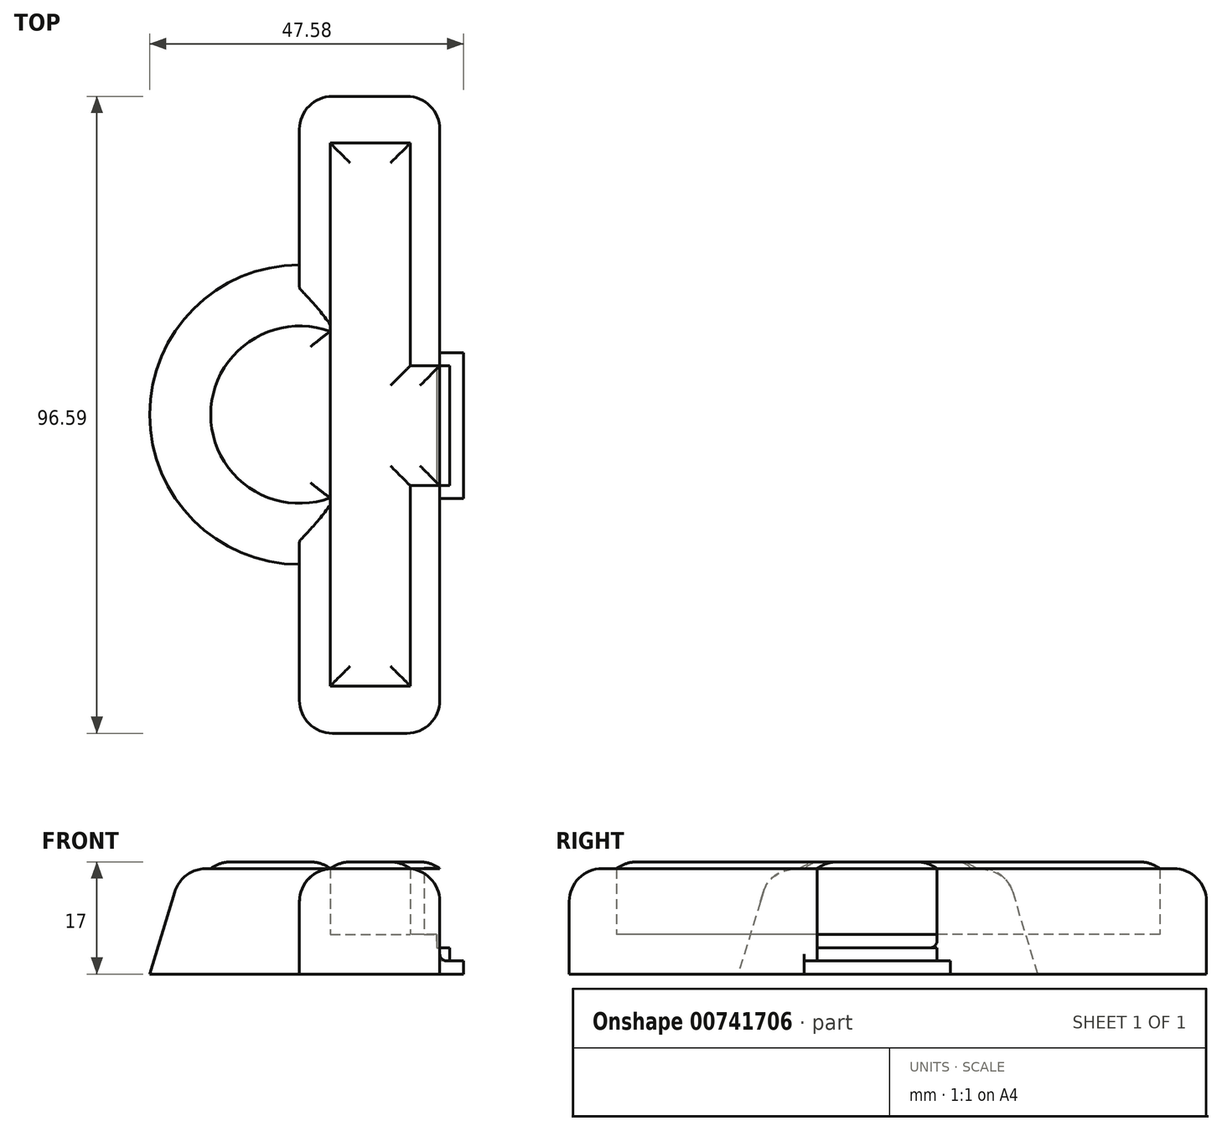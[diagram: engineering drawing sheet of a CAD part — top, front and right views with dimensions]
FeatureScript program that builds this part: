
annotation { "Feature Type Name" : "Feature", "Feature Type Description" : "" }
export const myFeature = defineFeature(function(context is Context, id is Id, definition is map)
    precondition{}
    {
        {
            var Q0;
            Q0=qCreatedBy(makeId("Top.planeOp"),FACE);
            var sketch = newSketch(context, id + "F0", { "sketchPlane" : qUnion([Q0])});
            skLineSegment(sketch, "E0.bottom", {"start": v(0, 48.27) * mm, "end": v(21.27, 48.27) * mm});
            skLineSegment(sketch, "E0.top", {"start": v(0, -48.32) * mm, "end": v(21.27, -48.32) * mm});
            skLineSegment(sketch, "E0.left", {"start": v(0, 48.27) * mm, "end": v(0, -48.32) * mm});
            skLineSegment(sketch, "E0.right", {"start": v(21.27, 48.27) * mm, "end": v(21.27, -48.32) * mm});
            skSolve(sketch);
        }
        {
            var Q0;
            Q0=makeQuery(id+"F0.imprint","IMPRINT",FACE,{"disambiguationData":[TD([[makeQuery(id+"F0.imprint","IMPRINT",EDGE,{"derivedFrom":sQuery(id+"F0.wireOp",EDGE,"E0.bottom")}),-1.0]])]});
            extrude(context, id + "F1", {"entities" : qUnion([Q0]), "depth" : 3 * mm, "offsetDistance" : 25 * mm});
        }
        {
            var Q0;
            Q0=makeQuery(id+"F1.opExtrude","CAP_FACE",FACE,{"disambiguationData":[OSD([sQuery(id+"F0.wireOp",EDGE,"E0.bottom"),sQuery(id+"F0.wireOp",EDGE,"E0.top"),sQuery(id+"F0.wireOp",EDGE,"E0.left"),sQuery(id+"F0.wireOp",EDGE,"E0.right")])],"isStart":false});
            var sketch = newSketch(context, id + "F2", { "sketchPlane" : qUnion([Q0])});
            skLineSegment(sketch, "E1.bottom", {"start": v(4.68, 41.18) * mm, "end": v(16.78, 41.18) * mm});
            skLineSegment(sketch, "E1.top", {"start": v(4.68, -41.14) * mm, "end": v(16.78, -41.14) * mm});
            skLineSegment(sketch, "E1.left", {"start": v(4.68, 41.18) * mm, "end": v(4.68, -41.14) * mm});
            skLineSegment(sketch, "E1.right", {"start": v(16.78, 41.18) * mm, "end": v(16.78, -41.14) * mm});
            skSolve(sketch);
        }
        {
            var Q0;
            Q0=makeQuery(id+"F2.imprint","IMPRINT",FACE,{"disambiguationData":[TD([[makeQuery(id+"F2.imprint","IMPRINT",EDGE,{"derivedFrom":sQuery(id+"F2.wireOp",EDGE,"E1.bottom")}),-1.0]])]});
            extrude(context, id + "F3", {"entities" : qUnion([Q0]), "operationType" : NewBodyOperationType.ADD, "depth" : 3 * mm, "offsetDistance" : 25 * mm});
        }
        {
            var Q0;
            Q0=makeQuery(id+"F2.imprint","IMPRINT",FACE,{"disambiguationData":[TD([[makeQuery(id+"F2.imprint","IMPRINT",EDGE,{"derivedFrom":sQuery(id+"F2.wireOp",EDGE,"E1.bottom")}),1.0]])]});
            var sketch = newSketch(context, id + "F4", { "sketchPlane" : qUnion([Q0])});
            skLineSegment(sketch, "E2.bottom", {"start": v(16.62, 7.41) * mm, "end": v(18.88, 7.41) * mm});
            skLineSegment(sketch, "E2.top", {"start": v(16.62, -10.75) * mm, "end": v(18.88, -10.75) * mm});
            skLineSegment(sketch, "E2.left", {"start": v(16.62, 7.41) * mm, "end": v(16.62, -10.75) * mm});
            skLineSegment(sketch, "E2.right", {"start": v(18.88, 7.41) * mm, "end": v(18.88, -10.75) * mm});
            skSolve(sketch);
        }
        {
            var Q0;
            {var subQ1=sQuery(id+"F4.wireOp",EDGE,"E2.right");Q0=makeQuery(id+"F4.imprint","IMPRINT",FACE,{"disambiguationData":[TD([[makeQuery(id+"F4.imprint","IMPRINT",EDGE,{"derivedFrom":subQ1}),1.0]])]});}
            extrude(context, id + "F5", {"entities" : qUnion([Q0]), "operationType" : NewBodyOperationType.ADD, "depth" : 13 * mm, "offsetDistance" : 25 * mm});
        }
        {
            var Q0;
            Q0=makeQuery(id+"F5.opExtrude","CAP_FACE",FACE,{"disambiguationData":[OSD([sQuery(id+"F0.wireOp",EDGE,"E0.bottom"),sQuery(id+"F0.wireOp",EDGE,"E0.top"),sQuery(id+"F0.wireOp",EDGE,"E0.left"),sQuery(id+"F0.wireOp",EDGE,"E0.right"),sQuery(id+"F2.wireOp",EDGE,"E1.bottom"),sQuery(id+"F2.wireOp",EDGE,"E1.top"),sQuery(id+"F2.wireOp",EDGE,"E1.left"),sQuery(id+"F2.wireOp",EDGE,"E1.right"),sQuery(id+"F4.wireOp",EDGE,"E2.bottom"),sQuery(id+"F4.wireOp",EDGE,"E2.top"),sQuery(id+"F4.wireOp",EDGE,"E2.right")])],"isStart":false});
            var sketch = newSketch(context, id + "F6", { "sketchPlane" : qUnion([Q0])});
            skArc(sketch, "E3", {"start": v(0, 17.81) * mm, "mid": v(-17.81, 0) * mm, "end": v(0, -17.81) * mm});
            skSolve(sketch);
        }
        {
            var Q0;
            {var subQ0=sQuery(id+"F6.wireOp",EDGE,"E3");Q0=makeQuery(id+"F6.imprint","IMPRINT",FACE,{"disambiguationData":[TD([[makeQuery(id+"F6.imprint","IMPRINT",EDGE,{"derivedFrom":subQ0}),1.0]])]});}
            extrude(context, id + "F7", {"entities" : qUnion([Q0]), "operationType" : NewBodyOperationType.ADD, "depth" : -16 * mm, "offsetDistance" : 25 * mm, "hasDraft" : true, "draftAngle" : 17 * degree});
        }
        {
            var Q0;
            {var subQ0=sQuery(id+"F0.wireOp",EDGE,"E0.left");Q0=makeQuery(id+"F7.boolean.opBoolean","MERGE",FACE,{"derivedFrom":[makeQuery(id+"F5.opExtrude","CAP_FACE",FACE,{"disambiguationData":[OSD([sQuery(id+"F0.wireOp",EDGE,"E0.bottom"),sQuery(id+"F0.wireOp",EDGE,"E0.top"),subQ0,sQuery(id+"F0.wireOp",EDGE,"E0.right"),sQuery(id+"F2.wireOp",EDGE,"E1.bottom"),sQuery(id+"F2.wireOp",EDGE,"E1.top"),sQuery(id+"F2.wireOp",EDGE,"E1.left"),sQuery(id+"F2.wireOp",EDGE,"E1.right"),sQuery(id+"F4.wireOp",EDGE,"E2.bottom"),sQuery(id+"F4.wireOp",EDGE,"E2.top"),sQuery(id+"F4.wireOp",EDGE,"E2.right")])],"isStart":false}),makeQuery(id+"F7.opExtrude","CAP_FACE",FACE,{"disambiguationData":[OSD([subQ0,sQuery(id+"F6.wireOp",EDGE,"E3")])],"isStart":true})]});}
            var sketch = newSketch(context, id + "F8", { "sketchPlane" : qUnion([Q0])});
            skLineSegment(sketch, "E4.bottom", {"start": v(18.88, 7.41) * mm, "end": v(21.27, 7.41) * mm});
            skLineSegment(sketch, "E4.top", {"start": v(18.88, -10.74) * mm, "end": v(21.27, -10.74) * mm});
            skLineSegment(sketch, "E4.left", {"start": v(18.88, 7.41) * mm, "end": v(18.88, -10.74) * mm});
            skLineSegment(sketch, "E4.right", {"start": v(21.27, 7.41) * mm, "end": v(21.27, -10.74) * mm});
            skSolve(sketch);
        }
        {
            var Q0;
            Q0=makeQuery(id+"F8.imprint","IMPRINT",FACE,{"disambiguationData":[TD([[makeQuery(id+"F8.imprint","IMPRINT",EDGE,{"derivedFrom":sQuery(id+"F8.wireOp",EDGE,"E4.bottom")}),-1.0]])]});
            extrude(context, id + "F9", {"entities" : qUnion([Q0]), "operationType" : NewBodyOperationType.REMOVE, "oppositeDirection" : true, "depth" : 25 * mm, "offsetDistance" : 25 * mm});
        }
        {
            var Q0;
            Q0=makeQuery(id+"F3.opExtrude","SWEPT_FACE",FACE,{"disambiguationData":[OSD([sQuery(id+"F2.wireOp",EDGE,"E1.right")])]});
            var Q1;
            Q1=makeQuery(id+"F9.boolean.opBoolean","COPY",FACE,{"derivedFrom":makeQuery(id+"F9.opExtrude","SWEPT_FACE",FACE,{"disambiguationData":[OSD([sQuery(id+"F8.wireOp",EDGE,"E4.left")])]})});
            extrude(context, id + "F10", {"entities" : qUnion([Q0, Q1]), "operationType" : NewBodyOperationType.ADD, "depth" : 6 * mm, "offsetDistance" : 25 * mm});
        }
        {
            var Q0;
            Q0=makeQuery(id+"F10.opExtrude","SWEPT_FACE",FACE,{"disambiguationData":[OSD([sQuery(id+"F4.wireOp",EDGE,"E2.right"),sQuery(id+"F8.wireOp",EDGE,"E4.top"),sQuery(id+"F8.wireOp",EDGE,"E4.left")])]});
            extrude(context, id + "F11", {"entities" : qUnion([Q0]), "operationType" : NewBodyOperationType.ADD, "depth" : 2 * mm, "offsetDistance" : 25 * mm});
        }
        {
            var Q0;
            {var subQ0=sQuery(id+"F4.wireOp",EDGE,"E2.bottom");Q0=makeQuery(id+"F10.boolean.opBoolean","MERGE",FACE,{"derivedFrom":[makeQuery(id+"F10.opExtrude","SWEPT_FACE",FACE,{"disambiguationData":[OSD([sQuery(id+"F2.wireOp",EDGE,"E1.right"),subQ0])]}),makeQuery(id+"F10.opExtrude","SWEPT_FACE",FACE,{"disambiguationData":[OSD([subQ0,sQuery(id+"F8.wireOp",EDGE,"E4.bottom"),sQuery(id+"F8.wireOp",EDGE,"E4.left")])]})]});}
            var sketch = newSketch(context, id + "F12", { "sketchPlane" : qUnion([Q0])});
            skLineSegment(sketch, "E5.bottom", {"start": v(-24.88, 3) * mm, "end": v(-21.27, 3) * mm});
            skLineSegment(sketch, "E5.top", {"start": v(-24.88, 0) * mm, "end": v(-21.27, 0) * mm});
            skLineSegment(sketch, "E5.left", {"start": v(-24.88, 3) * mm, "end": v(-24.88, 0) * mm});
            skLineSegment(sketch, "E5.right", {"start": v(-21.27, 3) * mm, "end": v(-21.27, 0) * mm});
            skSolve(sketch);
        }
        {
            var Q0;
            Q0=makeQuery(id+"F12.imprint","IMPRINT",FACE,{"disambiguationData":[TD([[makeQuery(id+"F12.imprint","IMPRINT",EDGE,{"derivedFrom":sQuery(id+"F12.wireOp",EDGE,"E5.top")}),1.0]])]});
            extrude(context, id + "F13", {"entities" : qUnion([Q0]), "operationType" : NewBodyOperationType.ADD, "depth" : 2 * mm, "offsetDistance" : 25 * mm});
        }
        {
            var Q0;
            {var subQ0=sQuery(id+"F2.wireOp",EDGE,"E1.right");var subQ1=makeQuery(id+"F3.opExtrude","CAP_FACE",FACE,{"disambiguationData":[OSD([sQuery(id+"F2.wireOp",EDGE,"E1.bottom"),sQuery(id+"F2.wireOp",EDGE,"E1.top"),sQuery(id+"F2.wireOp",EDGE,"E1.left"),subQ0])],"isStart":false});Q0=makeQuery(id+"F10.boolean.opBoolean","MERGE",FACE,{"derivedFrom":[subQ1,makeQuery(id+"F10.opExtrude","SWEPT_FACE",FACE,{"disambiguationData":[OSD([subQ0]),TDD([makeQuery(id+"F5.boolean.opBoolean","SPLIT",EDGE,{"disambiguationData":[topologyDisambiguationEdgeConnected([makeQuery(id+"F3.opExtrude","SWEPT_FACE",FACE,{"disambiguationData":[OSD([subQ0])]})])],"derivedFrom":makeQuery(id+"F3.opExtrude","CAP_EDGE",EDGE,{"disambiguationData":[OSD([subQ0])],"isStart":false})})])]})]});}
            var sketch = newSketch(context, id + "F14", { "sketchPlane" : qUnion([Q0])});
            skLineSegment(sketch, "E6.bottom", {"start": v(16.78, 7.41) * mm, "end": v(22.78, 7.41) * mm});
            skLineSegment(sketch, "E6.top", {"start": v(16.78, -10.75) * mm, "end": v(22.78, -10.75) * mm});
            skLineSegment(sketch, "E6.left", {"start": v(16.78, 7.41) * mm, "end": v(16.78, -10.75) * mm});
            skLineSegment(sketch, "E6.right", {"start": v(22.78, 7.41) * mm, "end": v(22.78, -10.75) * mm});
            skSolve(sketch);
        }
        {
            var Q0;
            {var subQ0=sQuery(id+"F14.wireOp",EDGE,"E6.left");Q0=makeQuery(id+"F14.imprint","IMPRINT",FACE,{"disambiguationData":[TD([[makeQuery(id+"F14.imprint","IMPRINT",EDGE,{"derivedFrom":subQ0}),1.0]])]});}
            extrude(context, id + "F15", {"entities" : qUnion([Q0]), "operationType" : NewBodyOperationType.REMOVE, "depth" : -2 * mm, "offsetDistance" : 25 * mm});
        }
        {
            var Q0;
            {var subQ0=sQuery(id+"F4.wireOp",EDGE,"E2.right");Q0=makeQuery(id+"F13.boolean.opBoolean","MERGE",FACE,{"derivedFrom":[makeQuery(id+"F11.boolean.opBoolean","MERGE",FACE,{"derivedFrom":[makeQuery(id+"F10.opExtrude","SWEPT_FACE",FACE,{"disambiguationData":[OSD([subQ0])]}),makeQuery(id+"F11.opExtrude","SWEPT_FACE",FACE,{"disambiguationData":[OSD([sQuery(id+"F0.wireOp",EDGE,"E0.bottom"),sQuery(id+"F0.wireOp",EDGE,"E0.top"),sQuery(id+"F0.wireOp",EDGE,"E0.left"),sQuery(id+"F0.wireOp",EDGE,"E0.right"),subQ0,sQuery(id+"F8.wireOp",EDGE,"E4.top"),sQuery(id+"F8.wireOp",EDGE,"E4.left")])]})]}),makeQuery(id+"F13.opExtrude","SWEPT_FACE",FACE,{"disambiguationData":[OSD([sQuery(id+"F12.wireOp",EDGE,"E5.bottom")])]})]});}
            extrude(context, id + "F16", {"entities" : qUnion([Q0]), "operationType" : NewBodyOperationType.REMOVE, "oppositeDirection" : true, "depth" : 1 * mm, "offsetDistance" : 25 * mm});
        }
        {
            var Q0;
            {var subQ0=sQuery(id+"F0.wireOp",EDGE,"E0.left");Q0=makeQuery(id+"F7.boolean.opBoolean","MERGE",FACE,{"derivedFrom":[makeQuery(id+"F5.opExtrude","CAP_FACE",FACE,{"disambiguationData":[OSD([sQuery(id+"F0.wireOp",EDGE,"E0.bottom"),sQuery(id+"F0.wireOp",EDGE,"E0.top"),subQ0,sQuery(id+"F0.wireOp",EDGE,"E0.right"),sQuery(id+"F2.wireOp",EDGE,"E1.bottom"),sQuery(id+"F2.wireOp",EDGE,"E1.top"),sQuery(id+"F2.wireOp",EDGE,"E1.left"),sQuery(id+"F2.wireOp",EDGE,"E1.right"),sQuery(id+"F4.wireOp",EDGE,"E2.bottom"),sQuery(id+"F4.wireOp",EDGE,"E2.top"),sQuery(id+"F4.wireOp",EDGE,"E2.right")])],"isStart":false}),makeQuery(id+"F7.opExtrude","CAP_FACE",FACE,{"disambiguationData":[OSD([subQ0,sQuery(id+"F6.wireOp",EDGE,"E3")])],"isStart":true})]});}
            var sketch = newSketch(context, id + "F17", { "sketchPlane" : qUnion([Q0])});
            skLineSegment(sketch, "E7.bottom", {"start": v(0, -48.32) * mm, "end": v(21.27, -48.32) * mm});
            skLineSegment(sketch, "E7.top", {"start": v(0, 48.27) * mm, "end": v(21.27, 48.27) * mm});
            skLineSegment(sketch, "E7.left", {"start": v(0, -48.32) * mm, "end": v(0, 48.27) * mm});
            skLineSegment(sketch, "E7.right", {"start": v(21.27, -48.32) * mm, "end": v(21.27, 48.27) * mm});
            skSolve(sketch);
        }
        {
            var Q0;
            Q0=makeQuery(id+"F15.boolean.opBoolean","COPY",FACE,{"derivedFrom":makeQuery(id+"F15.opExtrude","SWEPT_FACE",FACE,{"disambiguationData":[OSD([sQuery(id+"F14.wireOp",EDGE,"E6.left")])]})});
            extrude(context, id + "F18", {"entities" : qUnion([Q0]), "operationType" : NewBodyOperationType.ADD, "depth" : 4 * mm, "offsetDistance" : 25 * mm});
        }
        {
            var Q0;
            {var subQ2=sQuery(id+"F4.wireOp",EDGE,"E2.top");Q0=makeQuery(id+"F17.imprint","IMPRINT",FACE,{"disambiguationData":[TD([[makeQuery(id+"F17.imprint","IMPRINT",EDGE,{"derivedFrom":makeQuery(id+"F5.opExtrude","CAP_EDGE",EDGE,{"disambiguationData":[OSD([subQ2])],"isStart":false})}),1.0]])]});}
            extrude(context, id + "F19", {"entities" : qUnion([Q0]), "depth" : 1 * mm, "offsetDistance" : 25 * mm});
        }
        {
            var Q0;
            {var subQ0=sQuery(id+"F0.wireOp",EDGE,"E0.left");Q0=makeQuery(id+"F7.boolean.opBoolean","MERGE",FACE,{"derivedFrom":[makeQuery(id+"F5.opExtrude","CAP_FACE",FACE,{"disambiguationData":[OSD([sQuery(id+"F0.wireOp",EDGE,"E0.bottom"),sQuery(id+"F0.wireOp",EDGE,"E0.top"),subQ0,sQuery(id+"F0.wireOp",EDGE,"E0.right"),sQuery(id+"F2.wireOp",EDGE,"E1.bottom"),sQuery(id+"F2.wireOp",EDGE,"E1.top"),sQuery(id+"F2.wireOp",EDGE,"E1.left"),sQuery(id+"F2.wireOp",EDGE,"E1.right"),sQuery(id+"F4.wireOp",EDGE,"E2.bottom"),sQuery(id+"F4.wireOp",EDGE,"E2.top"),sQuery(id+"F4.wireOp",EDGE,"E2.right")])],"isStart":false}),makeQuery(id+"F7.opExtrude","CAP_FACE",FACE,{"disambiguationData":[OSD([subQ0,sQuery(id+"F6.wireOp",EDGE,"E3")])],"isStart":true})]});}
            var sketch = newSketch(context, id + "F20", { "sketchPlane" : qUnion([Q0])});
            skArc(sketch, "E8", {"start": v(4.68, 12.6) * mm, "mid": v(-13.44, 0) * mm, "end": v(4.68, -12.6) * mm});
            skSolve(sketch);
        }
        {
            var Q0;
            {var subQ0=sQuery(id+"F20.wireOp",EDGE,"E8");Q0=makeQuery(id+"F20.imprint","IMPRINT",FACE,{"disambiguationData":[TD([[makeQuery(id+"F20.imprint","IMPRINT",EDGE,{"derivedFrom":subQ0}),1.0]])]});}
            extrude(context, id + "F21", {"entities" : qUnion([Q0]), "depth" : 1 * mm, "offsetDistance" : 25 * mm});
        }
        {
            var Q0;
            {var subQ0=sQuery(id+"F0.wireOp",EDGE,"E0.right");var subQ1=sQuery(id+"F0.wireOp",EDGE,"E0.bottom");Q0=makeQuery(id+"F5.boolean.opBoolean","MERGE",EDGE,{"derivedFrom":[makeQuery(id+"F1.opExtrude","SWEPT_EDGE",EDGE,{"disambiguationData":[OSD([subQ1,subQ0])]}),makeQuery(id+"F5.opExtrude","SWEPT_EDGE",EDGE,{"disambiguationData":[OSD([subQ1,subQ0])]})]});}
            var Q1;
            Q1=makeQuery(id+"F5.opExtrude","CAP_EDGE",EDGE,{"disambiguationData":[OSD([sQuery(id+"F0.wireOp",EDGE,"E0.bottom")])],"isStart":false});
            var Q2;
            {var subQ1=sQuery(id+"F0.wireOp",EDGE,"E0.right");var subQ3=sQuery(id+"F0.wireOp",EDGE,"E0.bottom");Q2=makeQuery(id+"F9.boolean.opBoolean","SPLIT",EDGE,{"disambiguationData":[TD([makeQuery(id+"F1.opExtrude","SWEPT_FACE",FACE,{"disambiguationData":[OSD([subQ3])]})])],"derivedFrom":makeQuery(id+"F5.opExtrude","CAP_EDGE",EDGE,{"disambiguationData":[OSD([subQ1])],"isStart":false})});}
            var Q3;
            {var subQ0=sQuery(id+"F0.wireOp",EDGE,"E0.right");var subQ1=sQuery(id+"F0.wireOp",EDGE,"E0.top");Q3=makeQuery(id+"F5.boolean.opBoolean","MERGE",EDGE,{"derivedFrom":[makeQuery(id+"F1.opExtrude","SWEPT_EDGE",EDGE,{"disambiguationData":[OSD([subQ1,subQ0])]}),makeQuery(id+"F5.opExtrude","SWEPT_EDGE",EDGE,{"disambiguationData":[OSD([subQ1,subQ0])]})]});}
            var Q4;
            {var subQ0=sQuery(id+"F0.wireOp",EDGE,"E0.top");var subQ1=sQuery(id+"F0.wireOp",EDGE,"E0.right");Q4=makeQuery(id+"F9.boolean.opBoolean","SPLIT",EDGE,{"disambiguationData":[TD([makeQuery(id+"F1.opExtrude","SWEPT_FACE",FACE,{"disambiguationData":[OSD([subQ0])]})])],"derivedFrom":makeQuery(id+"F5.opExtrude","CAP_EDGE",EDGE,{"disambiguationData":[OSD([subQ1])],"isStart":false})});}
            var Q5;
            Q5=makeQuery(id+"F5.opExtrude","CAP_EDGE",EDGE,{"disambiguationData":[OSD([sQuery(id+"F0.wireOp",EDGE,"E0.top")])],"isStart":false});
            var Q6;
            {var subQ0=sQuery(id+"F0.wireOp",EDGE,"E0.left");var subQ1=sQuery(id+"F0.wireOp",EDGE,"E0.bottom");Q6=makeQuery(id+"F7.boolean.opBoolean","SPLIT",EDGE,{"disambiguationData":[TD([makeQuery(id+"F1.opExtrude","SWEPT_FACE",FACE,{"disambiguationData":[OSD([subQ1])]})])],"derivedFrom":makeQuery(id+"F5.opExtrude","CAP_EDGE",EDGE,{"disambiguationData":[OSD([subQ0])],"isStart":false})});}
            var Q7;
            {var subQ0=sQuery(id+"F0.wireOp",EDGE,"E0.left");var subQ1=sQuery(id+"F0.wireOp",EDGE,"E0.bottom");Q7=makeQuery(id+"F5.boolean.opBoolean","MERGE",EDGE,{"derivedFrom":[makeQuery(id+"F1.opExtrude","SWEPT_EDGE",EDGE,{"disambiguationData":[OSD([subQ1,subQ0])]}),makeQuery(id+"F5.opExtrude","SWEPT_EDGE",EDGE,{"disambiguationData":[OSD([subQ1,subQ0])]})]});}
            var Q8;
            {var subQ0=sQuery(id+"F0.wireOp",EDGE,"E0.top");var subQ1=sQuery(id+"F0.wireOp",EDGE,"E0.left");Q8=makeQuery(id+"F7.boolean.opBoolean","SPLIT",EDGE,{"disambiguationData":[TD([makeQuery(id+"F1.opExtrude","SWEPT_FACE",FACE,{"disambiguationData":[OSD([subQ0])]})])],"derivedFrom":makeQuery(id+"F5.opExtrude","CAP_EDGE",EDGE,{"disambiguationData":[OSD([subQ1])],"isStart":false})});}
            var Q9;
            {var subQ0=sQuery(id+"F0.wireOp",EDGE,"E0.left");var subQ1=sQuery(id+"F0.wireOp",EDGE,"E0.top");Q9=makeQuery(id+"F5.boolean.opBoolean","MERGE",EDGE,{"derivedFrom":[makeQuery(id+"F1.opExtrude","SWEPT_EDGE",EDGE,{"disambiguationData":[OSD([subQ1,subQ0])]}),makeQuery(id+"F5.opExtrude","SWEPT_EDGE",EDGE,{"disambiguationData":[OSD([subQ1,subQ0])]})]});}
            var Q10;
            Q10=makeQuery(id+"F7.opExtrude","CAP_EDGE",EDGE,{"disambiguationData":[OSD([sQuery(id+"F6.wireOp",EDGE,"E3")])],"isStart":true});
            var Q11;
            Q11=makeQuery(id+"F19.opExtrude","CAP_EDGE",EDGE,{"disambiguationData":[OSD([sQuery(id+"F17.wireOp",EDGE,"E7.right")])],"isStart":false});
            var Q12;
            {var subQ0=sQuery(id+"F2.wireOp",EDGE,"E1.right");var subQ1=makeQuery(id+"F2.imprint","IMPRINT",EDGE,{"derivedFrom":subQ0});Q12=makeQuery(id+"F19.opExtrude","CAP_EDGE",EDGE,{"disambiguationData":[OSD([subQ0]),TDD([makeQuery(id+"F17.imprint","IMPRINT",EDGE,{"derivedFrom":makeQuery(id+"F5.opExtrude","CAP_EDGE",EDGE,{"disambiguationData":[OSD([subQ0]),TDD([makeQuery(id+"F4.imprint","IMPRINT",EDGE,{"disambiguationData":[TD([[makeQuery(id+"F4.imprint","INTERSECT",VERTEX,{"derivedFrom":[makeQuery(id+"F2.imprint","IMPRINT",EDGE,{"derivedFrom":sQuery(id+"F2.wireOp",EDGE,"E1.bottom")}),subQ1]}),-1.0]])],"derivedFrom":subQ1})])],"isStart":false})})])],"isStart":false});}
            var Q13;
            Q13=makeQuery(id+"F19.opExtrude","CAP_EDGE",EDGE,{"disambiguationData":[OSD([sQuery(id+"F4.wireOp",EDGE,"E2.bottom"),sQuery(id+"F8.wireOp",EDGE,"E4.bottom")])],"isStart":false});
            var Q14;
            Q14=makeQuery(id+"F19.opExtrude","CAP_EDGE",EDGE,{"disambiguationData":[OSD([sQuery(id+"F2.wireOp",EDGE,"E1.bottom")])],"isStart":false});
            var Q15;
            {var subQ0=sQuery(id+"F2.wireOp",EDGE,"E1.right");var subQ1=makeQuery(id+"F2.imprint","IMPRINT",EDGE,{"derivedFrom":subQ0});Q15=makeQuery(id+"F19.opExtrude","CAP_EDGE",EDGE,{"disambiguationData":[OSD([subQ0]),TDD([makeQuery(id+"F17.imprint","IMPRINT",EDGE,{"derivedFrom":makeQuery(id+"F5.opExtrude","CAP_EDGE",EDGE,{"disambiguationData":[OSD([subQ0]),TDD([makeQuery(id+"F4.imprint","IMPRINT",EDGE,{"disambiguationData":[TD([[makeQuery(id+"F4.imprint","INTERSECT",VERTEX,{"derivedFrom":[makeQuery(id+"F2.imprint","IMPRINT",EDGE,{"derivedFrom":sQuery(id+"F2.wireOp",EDGE,"E1.top")}),subQ1]}),1.0]])],"derivedFrom":subQ1})])],"isStart":false})})])],"isStart":false});}
            var Q16;
            Q16=makeQuery(id+"F19.opExtrude","CAP_EDGE",EDGE,{"disambiguationData":[OSD([sQuery(id+"F2.wireOp",EDGE,"E1.top")])],"isStart":false});
            var Q17;
            Q17=makeQuery(id+"F19.opExtrude","CAP_EDGE",EDGE,{"disambiguationData":[OSD([sQuery(id+"F2.wireOp",EDGE,"E1.left")])],"isStart":false});
            var Q18;
            Q18=makeQuery(id+"F21.opExtrude","CAP_EDGE",EDGE,{"disambiguationData":[OSD([sQuery(id+"F20.wireOp",EDGE,"E8")])],"isStart":false});
            var Q19;
            Q19=makeQuery(id+"F19.opExtrude","CAP_EDGE",EDGE,{"disambiguationData":[OSD([sQuery(id+"F4.wireOp",EDGE,"E2.top")])],"isStart":false});
            var Q20;
            Q20=makeQuery(id+"F21.opExtrude","CAP_EDGE",EDGE,{"disambiguationData":[OSD([sQuery(id+"F2.wireOp",EDGE,"E1.left")])],"isStart":false});
            fillet(context, id + "F22", {"entities" : qUnion([Q0, Q1, Q2, Q3, Q4, Q5, Q6, Q7, Q8, Q9, Q10, Q11, Q12, Q13, Q14, Q15, Q16, Q17, Q18, Q19, Q20]), "radius" : 5 * mm, "tangentPropagation" : true, "allowEdgeOverflow" : false});
        }
        {
            var Q0;
            {var subQ0=sQuery(id+"F14.wireOp",EDGE,"E6.left");Q0=makeQuery(id+"F18.opExtrude","CAP_EDGE",EDGE,{"disambiguationData":[OSD([subQ0]),TDD([makeQuery(id+"F15.boolean.opBoolean","COPY",EDGE,{"derivedFrom":makeQuery(id+"F15.opExtrude","CAP_EDGE",EDGE,{"disambiguationData":[OSD([subQ0])],"isStart":true})})])],"isStart":false});}
            var Q1;
            Q1=makeQuery(id+"F15.boolean.opBoolean","COPY",EDGE,{"derivedFrom":makeQuery(id+"F15.opExtrude","CAP_EDGE",EDGE,{"disambiguationData":[OSD([sQuery(id+"F14.wireOp",EDGE,"E6.right")])],"isStart":false})});
            var Q2;
            Q2=makeQuery(id+"F16.boolean.opBoolean","COPY",EDGE,{"derivedFrom":makeQuery(id+"F16.opExtrude","CAP_EDGE",EDGE,{"disambiguationData":[OSD([sQuery(id+"F0.wireOp",EDGE,"E0.bottom"),sQuery(id+"F0.wireOp",EDGE,"E0.top"),sQuery(id+"F0.wireOp",EDGE,"E0.left"),sQuery(id+"F0.wireOp",EDGE,"E0.right"),sQuery(id+"F4.wireOp",EDGE,"E2.right"),sQuery(id+"F8.wireOp",EDGE,"E4.top"),sQuery(id+"F8.wireOp",EDGE,"E4.left"),sQuery(id+"F12.wireOp",EDGE,"E5.bottom"),sQuery(id+"F12.wireOp",EDGE,"E5.left")])],"isStart":false})});
            var Q3;
            Q3=makeQuery(id+"F16.boolean.opBoolean","COPY",EDGE,{"derivedFrom":makeQuery(id+"F16.opExtrude","CAP_EDGE",EDGE,{"disambiguationData":[OSD([sQuery(id+"F0.wireOp",EDGE,"E0.bottom"),sQuery(id+"F0.wireOp",EDGE,"E0.top"),sQuery(id+"F0.wireOp",EDGE,"E0.left"),sQuery(id+"F0.wireOp",EDGE,"E0.right"),sQuery(id+"F4.wireOp",EDGE,"E2.right"),sQuery(id+"F8.wireOp",EDGE,"E4.top"),sQuery(id+"F8.wireOp",EDGE,"E4.left")])],"isStart":false})});
            var Q4;
            {var subQ0=sQuery(id+"F12.wireOp",EDGE,"E5.bottom");Q4=makeQuery(id+"F16.boolean.opBoolean","COPY",EDGE,{"derivedFrom":makeQuery(id+"F16.opExtrude","CAP_EDGE",EDGE,{"disambiguationData":[OSD([subQ0]),TDD([makeQuery(id+"F13.opExtrude","CAP_EDGE",EDGE,{"disambiguationData":[OSD([subQ0])],"isStart":false})])],"isStart":false})});}
            var Q5;
            {var subQ0=sQuery(id+"F14.wireOp",EDGE,"E6.top");var subQ1=sQuery(id+"F2.wireOp",EDGE,"E1.right");var subQ5=sQuery(id+"F0.wireOp",EDGE,"E0.right");var subQ7=sQuery(id+"F0.wireOp",EDGE,"E0.top");Q5=makeQuery(id+"F15.boolean.opBoolean","COPY",EDGE,{"derivedFrom":makeQuery(id+"F15.opExtrude","CAP_EDGE",EDGE,{"disambiguationData":[OSD([subQ0]),TDD([makeQuery(id+"F14.imprint","IMPRINT",EDGE,{"disambiguationData":[TD([[makeQuery(id+"F14.imprint","INTERSECT",VERTEX,{"derivedFrom":[subQ0,sQuery(id+"F14.wireOp",EDGE,"E6.right")]}),-1.0],[makeQuery(id+"F14.imprint","INTERSECT",VERTEX,{"derivedFrom":[makeQuery(id+"F10.boolean.opBoolean","INTERSECT",EDGE,{"derivedFrom":[makeQuery(id+"F9.boolean.opBoolean","SPLIT",FACE,{"disambiguationData":[TD([makeQuery(id+"F1.opExtrude","SWEPT_FACE",FACE,{"disambiguationData":[OSD([subQ7])]})])],"derivedFrom":makeQuery(id+"F5.boolean.opBoolean","MERGE",FACE,{"derivedFrom":[makeQuery(id+"F1.opExtrude","SWEPT_FACE",FACE,{"disambiguationData":[OSD([subQ5])]}),makeQuery(id+"F5.opExtrude","SWEPT_FACE",FACE,{"disambiguationData":[OSD([subQ5])]})]})}),makeQuery(id+"F10.opExtrude","SWEPT_FACE",FACE,{"disambiguationData":[OSD([subQ1]),TDD([makeQuery(id+"F5.boolean.opBoolean","SPLIT",EDGE,{"disambiguationData":[topologyDisambiguationEdgeConnected([makeQuery(id+"F3.opExtrude","SWEPT_FACE",FACE,{"disambiguationData":[OSD([subQ1])]})])],"derivedFrom":makeQuery(id+"F3.opExtrude","CAP_EDGE",EDGE,{"disambiguationData":[OSD([subQ1])],"isStart":false})})])]})]}),subQ0]}),1.0]])],"derivedFrom":subQ0})])],"isStart":false})});}
            var Q6;
            {var subQ0=sQuery(id+"F4.wireOp",EDGE,"E2.bottom");var subQ1=sQuery(id+"F2.wireOp",EDGE,"E1.right");var subQ2=sQuery(id+"F14.wireOp",EDGE,"E6.bottom");Q6=makeQuery(id+"F15.boolean.opBoolean","COPY",EDGE,{"disambiguationData":[topologyDisambiguationEdgeConnected([makeQuery(id+"F10.opExtrude","SWEPT_FACE",FACE,{"disambiguationData":[OSD([subQ1,subQ0])]})])],"derivedFrom":makeQuery(id+"F15.opExtrude","CAP_EDGE",EDGE,{"disambiguationData":[OSD([subQ2])],"isStart":false})});}
            fillet(context, id + "F23", {"entities" : qUnion([Q0, Q1, Q2, Q3, Q4, Q5, Q6]), "radius" : 1 * mm, "tangentPropagation" : true, "allowEdgeOverflow" : false});
        }
    });
